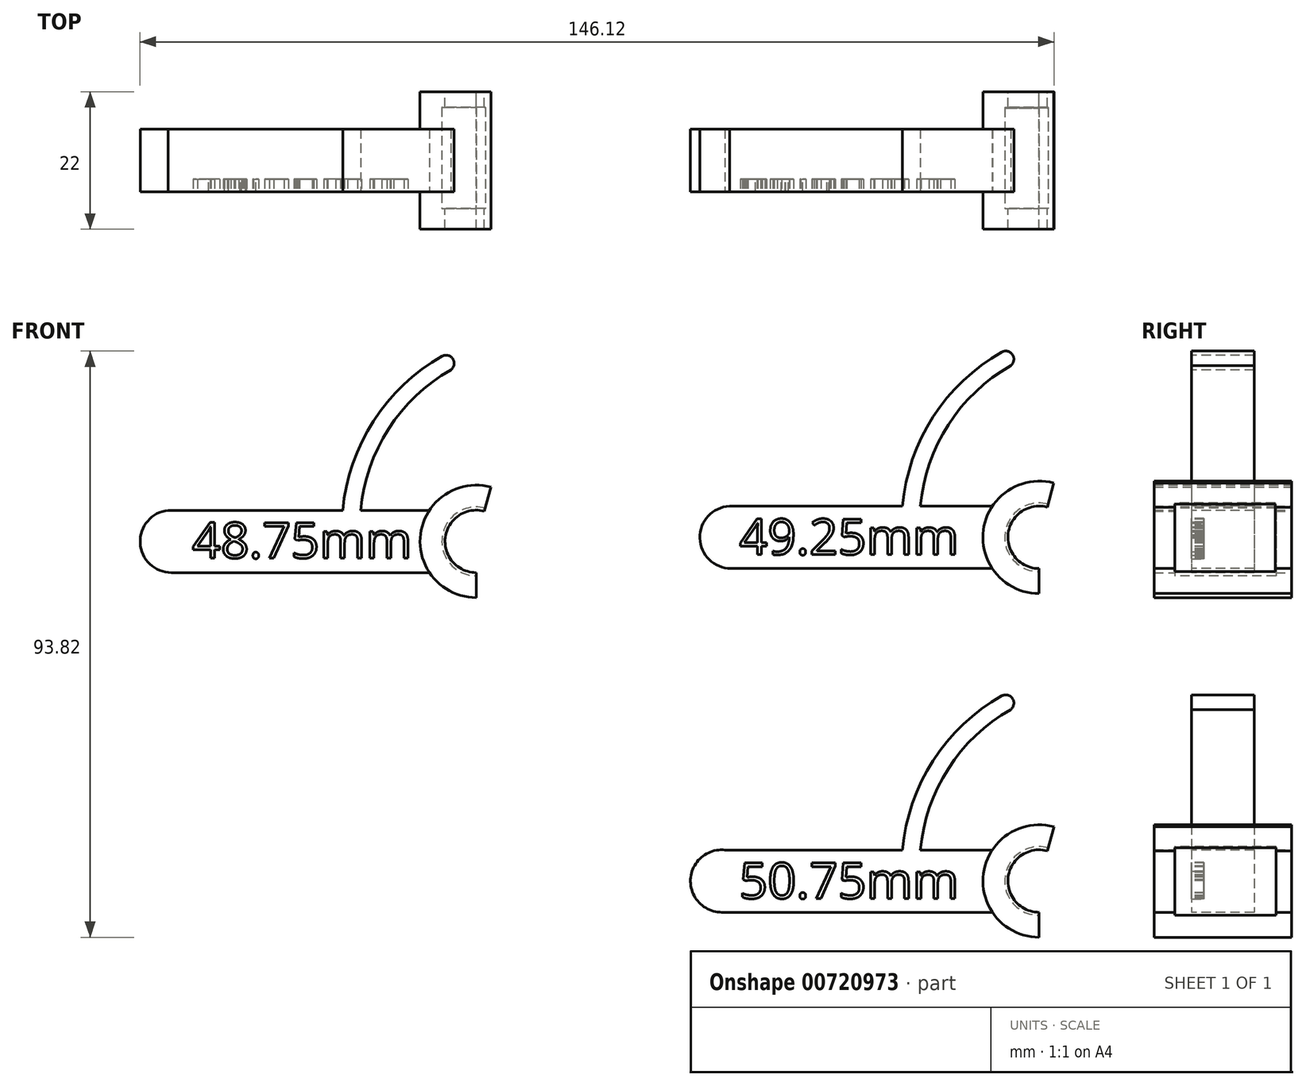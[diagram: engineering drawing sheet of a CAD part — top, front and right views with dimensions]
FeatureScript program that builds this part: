
annotation { "Feature Type Name" : "Feature", "Feature Type Description" : "" }
export const myFeature = defineFeature(function(context is Context, id is Id, definition is map)
    precondition{}
    {
        {
            var Q0;
            Q0=qCreatedBy(makeId("Front.planeOp"),FACE);
            var sketch = newSketch(context, id + "F0", { "sketchPlane" : qUnion([Q0])});
            skLineSegment(sketch, "E0.bottom", {"start": v(20.5, 25) * mm, "end": v(70.25, 25) * mm});
            skLineSegment(sketch, "E0.top", {"start": v(20.75, 15) * mm, "end": v(70, 15) * mm});
            skArc(sketch, "E1", {"start": v(20.5, 25) * mm, "mid": v(15.75, 19.88) * mm, "end": v(20.75, 15) * mm});
            skArc(sketch, "E2", {"start": v(71.29, 24.83) * mm, "mid": v(65.04, 20.65) * mm, "end": v(70, 15) * mm});
            skArc(sketch, "E3.0", {"start": v(72.32, 28.7) * mm, "mid": v(61.08, 21.17) * mm, "end": v(70, 11) * mm});
            skLineSegment(sketch, "E4", {"start": v(70.25, 29) * mm, "end": v(70.25, 25) * mm});
            skLineSegment(sketch, "E5", {"start": v(70, 15) * mm, "end": v(70, 11) * mm});
            skLineSegment(sketch, "E6.bottom", {"start": v(62.51, 25) * mm, "end": v(54.51, 25) * mm});
            skLineSegment(sketch, "E6.top", {"start": v(58.51, 37) * mm, "end": v(58.51, 37) * mm});
            skPoint(sketch, "E7.visualSharp", {"position": v(54.51, 37) * mm});
            skPoint(sketch, "E8.visualSharp", {"position": v(62.51, 37) * mm});
            skLineSegment(sketch, "E9", {"start": v(77.17, 20) * mm, "end": v(-0.92, 19.88) * mm, "construction": true});
            skPoint(sketch, "E9.endSnap0", {"position": v(15.75, 19.88) * mm});
            skLineSegment(sketch, "E10", {"start": v(70, 20) * mm, "end": v(72.32, 28.7) * mm});
            skArc(sketch, "E11", {"start": v(71.42, 25.31) * mm, "mid": v(64.55, 20.71) * mm, "end": v(70, 14.5) * mm});
            skArc(sketch, "E12", {"start": v(65.44, 47.47) * mm, "mid": v(55.47, 38) * mm, "end": v(51.02, 25) * mm});
            skArc(sketch, "E13", {"start": v(65.44, 47.47) * mm, "mid": v(65.74, 49.23) * mm, "end": v(64.01, 49.65) * mm});
            skArc(sketch, "E14", {"start": v(64.01, 49.65) * mm, "mid": v(53.04, 39.28) * mm, "end": v(48.15, 25) * mm});
            skLineSegment(sketch, "E15.bottom", {"start": v(19.75, -30.03) * mm, "end": v(69.5, -30.03) * mm});
            skLineSegment(sketch, "E15.top", {"start": v(19.24, -40) * mm, "end": v(70, -40) * mm});
            skArc(sketch, "E16", {"start": v(19.75, -30.03) * mm, "mid": v(14.25, -34.75) * mm, "end": v(19.24, -40) * mm});
            skArc(sketch, "E17", {"start": v(71.3, -30.17) * mm, "mid": v(65.04, -34.34) * mm, "end": v(70, -40) * mm});
            skArc(sketch, "E18.0", {"start": v(72.36, -26.31) * mm, "mid": v(61.08, -33.81) * mm, "end": v(70, -44) * mm});
            skLineSegment(sketch, "E19", {"start": v(70.25, -26) * mm, "end": v(69.5, -30.03) * mm});
            skLineSegment(sketch, "E20", {"start": v(70, -40) * mm, "end": v(70, -44) * mm});
            skLineSegment(sketch, "E21.bottom", {"start": v(62.5, -30.03) * mm, "end": v(54.5, -30.03) * mm});
            skLineSegment(sketch, "E21.top", {"start": v(17.58, -28.5) * mm, "end": v(17.58, -28.5) * mm});
            skPoint(sketch, "E22.visualSharp", {"position": v(54.5, -18.03) * mm});
            skPoint(sketch, "E23.visualSharp", {"position": v(62.5, -18.03) * mm});
            skLineSegment(sketch, "E24", {"start": v(77.17, -35) * mm, "end": v(-2.42, -34.75) * mm, "construction": true});
            skPoint(sketch, "E24.endSnap0", {"position": v(14.25, -34.75) * mm});
            skLineSegment(sketch, "E25", {"start": v(70, -35) * mm, "end": v(72.36, -26.31) * mm});
            skArc(sketch, "E26", {"start": v(71.44, -29.7) * mm, "mid": v(64.55, -34.27) * mm, "end": v(70, -40.5) * mm});
            skArc(sketch, "E27", {"start": v(65.44, -7.54) * mm, "mid": v(55.47, -17.01) * mm, "end": v(51.02, -30.03) * mm});
            skArc(sketch, "E28", {"start": v(65.44, -7.54) * mm, "mid": v(65.74, -5.79) * mm, "end": v(64.01, -5.37) * mm});
            skArc(sketch, "E29", {"start": v(64.01, -5.37) * mm, "mid": v(53.04, -15.74) * mm, "end": v(48.15, -30.03) * mm});
            skLineSegment(sketch, "E30.bottom", {"start": v(-69.25, 24.33) * mm, "end": v(-19.5, 24.33) * mm});
            skLineSegment(sketch, "E30.top", {"start": v(-68.76, 14.35) * mm, "end": v(-20, 14.35) * mm});
            skArc(sketch, "E31", {"start": v(-69.25, 24.33) * mm, "mid": v(-73.75, 19.1) * mm, "end": v(-68.76, 14.35) * mm});
            skArc(sketch, "E32", {"start": v(-18.7, 24.18) * mm, "mid": v(-24.96, 20) * mm, "end": v(-20, 14.35) * mm});
            skArc(sketch, "E33.0", {"start": v(-17.67, 28.04) * mm, "mid": v(-28.92, 20.53) * mm, "end": v(-20, 10.35) * mm});
            skLineSegment(sketch, "E34", {"start": v(-20, 14.35) * mm, "end": v(-20, 10.35) * mm});
            skLineSegment(sketch, "E35.bottom", {"start": v(-27.5, 24.33) * mm, "end": v(-35.5, 24.33) * mm});
            skLineSegment(sketch, "E35.top", {"start": v(-66.05, 60.12) * mm, "end": v(-66.05, 60.12) * mm});
            skPoint(sketch, "E36.visualSharp", {"position": v(-35.5, 36.33) * mm});
            skPoint(sketch, "E37.visualSharp", {"position": v(-27.5, 36.33) * mm});
            skPoint(sketch, "E38.endSnap0", {"position": v(-73.75, 19.1) * mm});
            skLineSegment(sketch, "E39", {"start": v(-20, 19.35) * mm, "end": v(-17.67, 28.04) * mm});
            skArc(sketch, "E40", {"start": v(-18.58, 24.66) * mm, "mid": v(-25.45, 20.07) * mm, "end": v(-20, 13.85) * mm});
            skArc(sketch, "E41", {"start": v(-24.06, 46.8) * mm, "mid": v(-34.04, 37.34) * mm, "end": v(-38.49, 24.33) * mm});
            skArc(sketch, "E42", {"start": v(-24.06, 46.8) * mm, "mid": v(-23.76, 48.56) * mm, "end": v(-25.5, 48.98) * mm});
            skArc(sketch, "E43", {"start": v(-25.5, 48.98) * mm, "mid": v(-36.46, 38.6) * mm, "end": v(-41.35, 24.33) * mm});
            skLineSegment(sketch, "E44", {"start": v(-15.27, 19.35) * mm, "end": v(-80.35, 19.35) * mm, "construction": true});
            skSolve(sketch);
        }
        {
            var Q0;
            {var subQ0=sQuery(id+"F0.wireOp",EDGE,"E5");Q0=makeQuery(id+"F0.imprint","IMPRINT",FACE,{"disambiguationData":[TD([[makeQuery(id+"F0.imprint","IMPRINT",EDGE,{"derivedFrom":subQ0}),-1.0]])]});}
            var Q1;
            {var subQ0=sQuery(id+"F0.wireOp",EDGE,"E2");Q1=makeQuery(id+"F0.imprint","IMPRINT",FACE,{"disambiguationData":[TD([[makeQuery(id+"F0.imprint","IMPRINT",EDGE,{"derivedFrom":subQ0}),-1.0]])]});}
            var Q2;
            {var subQ0=sQuery(id+"F0.wireOp",EDGE,"E4");Q2=makeQuery(id+"F0.imprint","IMPRINT",FACE,{"disambiguationData":[TD([[makeQuery(id+"F0.imprint","IMPRINT",EDGE,{"derivedFrom":subQ0}),-1.0]])]});}
            var Q3;
            {var subQ0=sQuery(id+"F0.wireOp",EDGE,"E10");var subQ1=sQuery(id+"F0.wireOp",EDGE,"E3.0");var subQ2=makeQuery(id+"F0.imprint","INTERSECT",VERTEX,{"derivedFrom":[subQ1,subQ0]});Q3=makeQuery(id+"F0.imprint","IMPRINT",FACE,{"disambiguationData":[TD([[makeQuery(id+"F0.imprint","IMPRINT",EDGE,{"disambiguationData":[TD([[subQ2,-1.0]])],"derivedFrom":subQ1}),1.0]])]});}
            var Q4;
            {var subQ0=sQuery(id+"F0.wireOp",EDGE,"E3.0");var subQ5=sQuery(id+"F0.wireOp",EDGE,"E0.top");var subQ6=makeQuery(id+"F0.imprint","INTERSECT",VERTEX,{"derivedFrom":[subQ5,subQ0]});Q4=makeQuery(id+"F0.imprint","IMPRINT",FACE,{"disambiguationData":[TD([[makeQuery(id+"F0.imprint","IMPRINT",EDGE,{"disambiguationData":[TD([[subQ6,-1.0]])],"derivedFrom":subQ5}),1.0]])]});}
            var Q5;
            {var subQ0=sQuery(id+"F0.wireOp",EDGE,"E3.0");var subQ1=sQuery(id+"F0.wireOp",EDGE,"E0.top");var subQ2=makeQuery(id+"F0.imprint","INTERSECT",VERTEX,{"derivedFrom":[subQ1,subQ0]});Q5=makeQuery(id+"F0.imprint","IMPRINT",FACE,{"disambiguationData":[TD([[makeQuery(id+"F0.imprint","IMPRINT",EDGE,{"disambiguationData":[TD([[subQ2,-1.0]])],"derivedFrom":subQ1}),-1.0]])]});}
            extrude(context, id + "F1", {"entities" : qUnion([Q0, Q1, Q2, Q3, Q4, Q5]), "depth" : 6 * mm, "offsetDistance" : 25 * mm, "hasSecondDirection" : true, "secondDirectionOppositeDirection" : true, "secondDirectionDepth" : 16 * mm});
        }
        {
            var Q0;
            {var subQ0=sQuery(id+"F0.wireOp",EDGE,"E1");Q0=makeQuery(id+"F0.imprint","IMPRINT",FACE,{"disambiguationData":[TD([[makeQuery(id+"F0.imprint","IMPRINT",EDGE,{"derivedFrom":subQ0}),1.0]])]});}
            var Q1;
            {var subQ0=sQuery(id+"F0.wireOp",EDGE,"E12");Q1=makeQuery(id+"F0.imprint","IMPRINT",FACE,{"disambiguationData":[TD([[makeQuery(id+"F0.imprint","IMPRINT",EDGE,{"derivedFrom":subQ0}),-1.0]])]});}
            extrude(context, id + "F2", {"entities" : qUnion([Q0, Q1]), "operationType" : NewBodyOperationType.ADD, "oppositeDirection" : true, "depth" : 10 * mm, "offsetDistance" : 25 * mm});
        }
        {
            var Q0;
            {var subQ0=sQuery(id+"F0.wireOp",EDGE,"E2");var subQ1=sQuery(id+"F0.wireOp",EDGE,"E0.bottom");var subQ2=makeQuery(id+"F0.imprint","INTERSECT",VERTEX,{"derivedFrom":[subQ1,subQ0]});Q0=makeQuery(id+"F0.imprint","IMPRINT",FACE,{"disambiguationData":[TD([[makeQuery(id+"F0.imprint","IMPRINT",EDGE,{"disambiguationData":[TD([[subQ2,1.0]])],"derivedFrom":subQ1}),-1.0]])]});}
            var Q1;
            {var subQ0=sQuery(id+"F0.wireOp",EDGE,"E5");var subQ3=sQuery(id+"F0.wireOp",EDGE,"E11");var subQ5=makeQuery(id+"F0.imprint","INTERSECT",VERTEX,{"derivedFrom":[subQ0,subQ3]});Q1=makeQuery(id+"F0.imprint","IMPRINT",FACE,{"disambiguationData":[TD([[makeQuery(id+"F0.imprint","IMPRINT",EDGE,{"disambiguationData":[TD([[subQ5,1.0]])],"derivedFrom":subQ3}),1.0]])]});}
            var Q2;
            {var subQ0=sQuery(id+"F0.wireOp",EDGE,"E2");var subQ1=sQuery(id+"F0.wireOp",EDGE,"E0.bottom");var subQ2=makeQuery(id+"F0.imprint","INTERSECT",VERTEX,{"derivedFrom":[subQ1,subQ0]});Q2=makeQuery(id+"F0.imprint","IMPRINT",FACE,{"disambiguationData":[TD([[makeQuery(id+"F0.imprint","IMPRINT",EDGE,{"disambiguationData":[TD([[subQ2,1.0]])],"derivedFrom":subQ1}),1.0]])]});}
            var Q3;
            {var subQ1=sQuery(id+"F0.wireOp",EDGE,"E2");var subQ3=sQuery(id+"F0.wireOp",EDGE,"E10");var subQ4=makeQuery(id+"F0.imprint","INTERSECT",VERTEX,{"derivedFrom":[subQ1,subQ3]});Q3=makeQuery(id+"F0.imprint","IMPRINT",FACE,{"disambiguationData":[TD([[makeQuery(id+"F0.imprint","IMPRINT",EDGE,{"disambiguationData":[TD([[subQ4,-1.0]])],"derivedFrom":subQ3}),1.0]])]});}
            extrude(context, id + "F3", {"entities" : qUnion([Q0, Q1, Q2, Q3]), "operationType" : NewBodyOperationType.REMOVE, "oppositeDirection" : true, "depth" : 13.4 * mm, "offsetDistance" : 25 * mm, "hasSecondDirection" : true, "secondDirectionOppositeDirection" : false, "secondDirectionDepth" : 2.7 * mm});
        }
        {
            var Q0;
            {var subQ3=sQuery(id+"F0.wireOp",EDGE,"E1");Q0=makeQuery(id+"F0.imprint","IMPRINT",FACE,{"disambiguationData":[TD([[makeQuery(id+"F0.imprint","IMPRINT",EDGE,{"derivedFrom":subQ3}),1.0]])]});}
            var sketch = newSketch(context, id + "F4", { "sketchPlane" : qUnion([Q0])});
            skText(sketch, "E45", { "text": "49.25mm", "fontName": "OpenSans-Regular.ttf"});
            const initialGuessF4  = {"E45": [0.02204, 0.01725, 1, 0, 0.00573]};
            skSetInitialGuess(sketch, initialGuessF4);
            skSolve(sketch);
        }
        {
            var Q0;
            Q0 = qSketchRegion(id + "F4", true);
            var Q1;
            Q1 = qConstructionFilter(qBodyType(qCreatedBy(id + "F4" ,EDGE), BodyType.WIRE), ConstructionObject.NO);
            extrude(context, id + "F5", {"entities" : qUnion([Q0]), "operationType" : NewBodyOperationType.REMOVE, "surfaceEntities" : qUnion([Q1]), "oppositeDirection" : true, "depth" : 2 * mm, "offsetDistance" : 25 * mm});
        }
        {
            var Q0;
            {var subQ0=sQuery(id+"F0.wireOp",EDGE,"E25");var subQ1=sQuery(id+"F0.wireOp",EDGE,"E18.0");var subQ2=makeQuery(id+"F0.imprint","INTERSECT",VERTEX,{"derivedFrom":[subQ1,subQ0]});Q0=makeQuery(id+"F0.imprint","IMPRINT",FACE,{"disambiguationData":[TD([[makeQuery(id+"F0.imprint","IMPRINT",EDGE,{"disambiguationData":[TD([[subQ2,-1.0]])],"derivedFrom":subQ1}),1.0]])]});}
            var Q1;
            {var subQ0=sQuery(id+"F0.wireOp",EDGE,"E18.0");var subQ5=sQuery(id+"F0.wireOp",EDGE,"E19");var subQ7=makeQuery(id+"F0.imprint","INTERSECT",VERTEX,{"derivedFrom":[subQ0,subQ5]});Q1=makeQuery(id+"F0.imprint","IMPRINT",FACE,{"disambiguationData":[TD([[makeQuery(id+"F0.imprint","IMPRINT",EDGE,{"disambiguationData":[TD([[subQ7,-1.0]])],"derivedFrom":subQ5}),-1.0]])]});}
            var Q2;
            {var subQ0=sQuery(id+"F0.wireOp",EDGE,"E18.0");var subQ5=sQuery(id+"F0.wireOp",EDGE,"E15.top");var subQ6=makeQuery(id+"F0.imprint","INTERSECT",VERTEX,{"derivedFrom":[subQ5,subQ0]});Q2=makeQuery(id+"F0.imprint","IMPRINT",FACE,{"disambiguationData":[TD([[makeQuery(id+"F0.imprint","IMPRINT",EDGE,{"disambiguationData":[TD([[subQ6,-1.0]])],"derivedFrom":subQ5}),1.0]])]});}
            var Q3;
            {var subQ0=sQuery(id+"F0.wireOp",EDGE,"E18.0");var subQ1=sQuery(id+"F0.wireOp",EDGE,"E15.top");var subQ2=makeQuery(id+"F0.imprint","INTERSECT",VERTEX,{"derivedFrom":[subQ1,subQ0]});Q3=makeQuery(id+"F0.imprint","IMPRINT",FACE,{"disambiguationData":[TD([[makeQuery(id+"F0.imprint","IMPRINT",EDGE,{"disambiguationData":[TD([[subQ2,-1.0]])],"derivedFrom":subQ1}),-1.0]])]});}
            var Q4;
            {var subQ0=sQuery(id+"F0.wireOp",EDGE,"E20");var subQ3=sQuery(id+"F0.wireOp",EDGE,"E26");var subQ5=makeQuery(id+"F0.imprint","INTERSECT",VERTEX,{"derivedFrom":[subQ0,subQ3]});Q4=makeQuery(id+"F0.imprint","IMPRINT",FACE,{"disambiguationData":[TD([[makeQuery(id+"F0.imprint","IMPRINT",EDGE,{"disambiguationData":[TD([[subQ5,1.0]])],"derivedFrom":subQ3}),1.0]])]});}
            var Q5;
            {var subQ1=sQuery(id+"F0.wireOp",EDGE,"E15.bottom");var subQ3=sQuery(id+"F0.wireOp",EDGE,"E26");var subQ4=makeQuery(id+"F0.imprint","INTERSECT",VERTEX,{"derivedFrom":[subQ1,subQ3]});Q5=makeQuery(id+"F0.imprint","IMPRINT",FACE,{"disambiguationData":[TD([[makeQuery(id+"F0.imprint","IMPRINT",EDGE,{"disambiguationData":[TD([[subQ4,-1.0]])],"derivedFrom":subQ3}),1.0]])]});}
            var Q6;
            {var subQ1=sQuery(id+"F0.wireOp",EDGE,"E15.bottom");var subQ3=sQuery(id+"F0.wireOp",EDGE,"E26");var subQ4=makeQuery(id+"F0.imprint","INTERSECT",VERTEX,{"derivedFrom":[subQ1,subQ3]});Q6=makeQuery(id+"F0.imprint","IMPRINT",FACE,{"disambiguationData":[TD([[makeQuery(id+"F0.imprint","IMPRINT",EDGE,{"disambiguationData":[TD([[subQ4,1.0]])],"derivedFrom":subQ3}),1.0]])]});}
            var Q7;
            {var subQ1=sQuery(id+"F0.wireOp",EDGE,"E17");var subQ3=sQuery(id+"F0.wireOp",EDGE,"E25");var subQ4=makeQuery(id+"F0.imprint","INTERSECT",VERTEX,{"derivedFrom":[subQ1,subQ3]});Q7=makeQuery(id+"F0.imprint","IMPRINT",FACE,{"disambiguationData":[TD([[makeQuery(id+"F0.imprint","IMPRINT",EDGE,{"disambiguationData":[TD([[subQ4,-1.0]])],"derivedFrom":subQ3}),1.0]])]});}
            extrude(context, id + "F6", {"entities" : qUnion([Q0, Q1, Q2, Q3, Q4, Q5, Q6, Q7]), "depth" : 6 * mm, "offsetDistance" : 25 * mm, "hasSecondDirection" : true, "secondDirectionOppositeDirection" : true, "secondDirectionDepth" : 16 * mm});
        }
        {
            var Q0;
            {var subQ7=sQuery(id+"F0.wireOp",EDGE,"E16");Q0=makeQuery(id+"F0.imprint","IMPRINT",FACE,{"disambiguationData":[TD([[makeQuery(id+"F0.imprint","IMPRINT",EDGE,{"derivedFrom":subQ7}),1.0]])]});}
            var Q1;
            {var subQ0=sQuery(id+"F0.wireOp",EDGE,"E27");Q1=makeQuery(id+"F0.imprint","IMPRINT",FACE,{"disambiguationData":[TD([[makeQuery(id+"F0.imprint","IMPRINT",EDGE,{"derivedFrom":subQ0}),-1.0]])]});}
            extrude(context, id + "F7", {"entities" : qUnion([Q0, Q1]), "operationType" : NewBodyOperationType.ADD, "oppositeDirection" : true, "depth" : 10 * mm, "offsetDistance" : 25 * mm});
        }
        {
            var Q0;
            {var subQ1=sQuery(id+"F0.wireOp",EDGE,"E17");var subQ3=sQuery(id+"F0.wireOp",EDGE,"E25");var subQ4=makeQuery(id+"F0.imprint","INTERSECT",VERTEX,{"derivedFrom":[subQ1,subQ3]});Q0=makeQuery(id+"F0.imprint","IMPRINT",FACE,{"disambiguationData":[TD([[makeQuery(id+"F0.imprint","IMPRINT",EDGE,{"disambiguationData":[TD([[subQ4,-1.0]])],"derivedFrom":subQ3}),1.0]])]});}
            var Q1;
            {var subQ1=sQuery(id+"F0.wireOp",EDGE,"E15.bottom");var subQ3=sQuery(id+"F0.wireOp",EDGE,"E26");var subQ4=makeQuery(id+"F0.imprint","INTERSECT",VERTEX,{"derivedFrom":[subQ1,subQ3]});Q1=makeQuery(id+"F0.imprint","IMPRINT",FACE,{"disambiguationData":[TD([[makeQuery(id+"F0.imprint","IMPRINT",EDGE,{"disambiguationData":[TD([[subQ4,1.0]])],"derivedFrom":subQ3}),1.0]])]});}
            var Q2;
            {var subQ1=sQuery(id+"F0.wireOp",EDGE,"E15.bottom");var subQ3=sQuery(id+"F0.wireOp",EDGE,"E26");var subQ4=makeQuery(id+"F0.imprint","INTERSECT",VERTEX,{"derivedFrom":[subQ1,subQ3]});Q2=makeQuery(id+"F0.imprint","IMPRINT",FACE,{"disambiguationData":[TD([[makeQuery(id+"F0.imprint","IMPRINT",EDGE,{"disambiguationData":[TD([[subQ4,-1.0]])],"derivedFrom":subQ3}),1.0]])]});}
            var Q3;
            {var subQ0=sQuery(id+"F0.wireOp",EDGE,"E20");var subQ3=sQuery(id+"F0.wireOp",EDGE,"E26");var subQ5=makeQuery(id+"F0.imprint","INTERSECT",VERTEX,{"derivedFrom":[subQ0,subQ3]});Q3=makeQuery(id+"F0.imprint","IMPRINT",FACE,{"disambiguationData":[TD([[makeQuery(id+"F0.imprint","IMPRINT",EDGE,{"disambiguationData":[TD([[subQ5,1.0]])],"derivedFrom":subQ3}),1.0]])]});}
            extrude(context, id + "F8", {"entities" : qUnion([Q0, Q1, Q2, Q3]), "operationType" : NewBodyOperationType.REMOVE, "oppositeDirection" : true, "depth" : 13.5 * mm, "offsetDistance" : 25 * mm, "hasSecondDirection" : true, "secondDirectionOppositeDirection" : false, "secondDirectionDepth" : 2.7 * mm});
        }
        {
            var Q0;
            {var subQ7=sQuery(id+"F0.wireOp",EDGE,"E16");Q0=makeQuery(id+"F0.imprint","IMPRINT",FACE,{"disambiguationData":[TD([[makeQuery(id+"F0.imprint","IMPRINT",EDGE,{"derivedFrom":subQ7}),1.0]])]});}
            var sketch = newSketch(context, id + "F9", { "sketchPlane" : qUnion([Q0])});
            skText(sketch, "E46", { "text": "50.75mm", "fontName": "OpenSans-Regular.ttf"});
            const initialGuessF9  = {"E46": [0.02204, -0.03778, 1, 0, 0.00573]};
            skSetInitialGuess(sketch, initialGuessF9);
            skSolve(sketch);
        }
        {
            var Q0;
            Q0 = qSketchRegion(id + "F9", true);
            extrude(context, id + "F10", {"entities" : qUnion([Q0]), "operationType" : NewBodyOperationType.REMOVE, "oppositeDirection" : true, "depth" : 2 * mm, "offsetDistance" : 25 * mm});
        }
        {
            var Q0;
            {var subQ0=sQuery(id+"F0.wireOp",EDGE,"E32");var subQ1=sQuery(id+"F0.wireOp",EDGE,"E30.bottom");var subQ3=makeQuery(id+"F0.imprint","INTERSECT",VERTEX,{"disambiguationData":[OD(1.0)],"derivedFrom":[subQ1,subQ0]});Q0=makeQuery(id+"F0.imprint","IMPRINT",FACE,{"disambiguationData":[TD([[makeQuery(id+"F0.imprint","IMPRINT",EDGE,{"disambiguationData":[TD([[subQ3,1.0]])],"derivedFrom":subQ1}),1.0]])]});}
            var Q1;
            {var subQ0=sQuery(id+"F0.wireOp",EDGE,"E32");var subQ1=sQuery(id+"F0.wireOp",EDGE,"E30.bottom");var subQ2=makeQuery(id+"F0.imprint","INTERSECT",VERTEX,{"disambiguationData":[OD(1.0)],"derivedFrom":[subQ1,subQ0]});Q1=makeQuery(id+"F0.imprint","IMPRINT",FACE,{"disambiguationData":[TD([[makeQuery(id+"F0.imprint","IMPRINT",EDGE,{"disambiguationData":[TD([[subQ2,1.0]])],"derivedFrom":subQ1}),-1.0]])]});}
            var Q2;
            {var subQ0=sQuery(id+"F0.wireOp",EDGE,"E34");var subQ3=sQuery(id+"F0.wireOp",EDGE,"E40");var subQ5=makeQuery(id+"F0.imprint","INTERSECT",VERTEX,{"derivedFrom":[subQ0,subQ3]});Q2=makeQuery(id+"F0.imprint","IMPRINT",FACE,{"disambiguationData":[TD([[makeQuery(id+"F0.imprint","IMPRINT",EDGE,{"disambiguationData":[TD([[subQ5,1.0]])],"derivedFrom":subQ3}),1.0]])]});}
            var Q3;
            {var subQ0=sQuery(id+"F0.wireOp",EDGE,"E33.0");var subQ1=sQuery(id+"F0.wireOp",EDGE,"E30.top");var subQ2=makeQuery(id+"F0.imprint","INTERSECT",VERTEX,{"derivedFrom":[subQ1,subQ0]});Q3=makeQuery(id+"F0.imprint","IMPRINT",FACE,{"disambiguationData":[TD([[makeQuery(id+"F0.imprint","IMPRINT",EDGE,{"disambiguationData":[TD([[subQ2,-1.0]])],"derivedFrom":subQ1}),-1.0]])]});}
            var Q4;
            {var subQ0=sQuery(id+"F0.wireOp",EDGE,"E33.0");var subQ5=sQuery(id+"F0.wireOp",EDGE,"E30.top");var subQ6=makeQuery(id+"F0.imprint","INTERSECT",VERTEX,{"derivedFrom":[subQ5,subQ0]});Q4=makeQuery(id+"F0.imprint","IMPRINT",FACE,{"disambiguationData":[TD([[makeQuery(id+"F0.imprint","IMPRINT",EDGE,{"disambiguationData":[TD([[subQ6,-1.0]])],"derivedFrom":subQ5}),1.0]])]});}
            var Q5;
            {var subQ0=sQuery(id+"F0.wireOp",EDGE,"E33.0");var subQ5=sQuery(id+"F0.wireOp",EDGE,"E39");var subQ6=makeQuery(id+"F0.imprint","INTERSECT",VERTEX,{"derivedFrom":[subQ0,subQ5]});Q5=makeQuery(id+"F0.imprint","IMPRINT",FACE,{"disambiguationData":[TD([[makeQuery(id+"F0.imprint","IMPRINT",EDGE,{"disambiguationData":[TD([[subQ6,1.0]])],"derivedFrom":subQ5}),1.0]])]});}
            extrude(context, id + "F11", {"entities" : qUnion([Q0, Q1, Q2, Q3, Q4, Q5]), "depth" : 6 * mm, "offsetDistance" : 25 * mm, "hasSecondDirection" : true, "secondDirectionOppositeDirection" : true, "secondDirectionDepth" : 16 * mm});
        }
        {
            var Q0;
            {var subQ3=sQuery(id+"F0.wireOp",EDGE,"E31");Q0=makeQuery(id+"F0.imprint","IMPRINT",FACE,{"disambiguationData":[TD([[makeQuery(id+"F0.imprint","IMPRINT",EDGE,{"derivedFrom":subQ3}),1.0]])]});}
            var Q1;
            {var subQ0=sQuery(id+"F0.wireOp",EDGE,"E41");Q1=makeQuery(id+"F0.imprint","IMPRINT",FACE,{"disambiguationData":[TD([[makeQuery(id+"F0.imprint","IMPRINT",EDGE,{"derivedFrom":subQ0}),-1.0]])]});}
            extrude(context, id + "F12", {"entities" : qUnion([Q0, Q1]), "operationType" : NewBodyOperationType.ADD, "oppositeDirection" : true, "depth" : 10 * mm, "offsetDistance" : 25 * mm});
        }
        {
            var Q0;
            {var subQ0=sQuery(id+"F0.wireOp",EDGE,"E34");var subQ3=sQuery(id+"F0.wireOp",EDGE,"E40");var subQ5=makeQuery(id+"F0.imprint","INTERSECT",VERTEX,{"derivedFrom":[subQ0,subQ3]});Q0=makeQuery(id+"F0.imprint","IMPRINT",FACE,{"disambiguationData":[TD([[makeQuery(id+"F0.imprint","IMPRINT",EDGE,{"disambiguationData":[TD([[subQ5,1.0]])],"derivedFrom":subQ3}),1.0]])]});}
            var Q1;
            {var subQ0=sQuery(id+"F0.wireOp",EDGE,"E32");var subQ1=sQuery(id+"F0.wireOp",EDGE,"E30.bottom");var subQ2=makeQuery(id+"F0.imprint","INTERSECT",VERTEX,{"disambiguationData":[OD(1.0)],"derivedFrom":[subQ1,subQ0]});Q1=makeQuery(id+"F0.imprint","IMPRINT",FACE,{"disambiguationData":[TD([[makeQuery(id+"F0.imprint","IMPRINT",EDGE,{"disambiguationData":[TD([[subQ2,1.0]])],"derivedFrom":subQ1}),-1.0]])]});}
            var Q2;
            {var subQ0=sQuery(id+"F0.wireOp",EDGE,"E32");var subQ1=sQuery(id+"F0.wireOp",EDGE,"E30.bottom");var subQ3=makeQuery(id+"F0.imprint","INTERSECT",VERTEX,{"disambiguationData":[OD(1.0)],"derivedFrom":[subQ1,subQ0]});Q2=makeQuery(id+"F0.imprint","IMPRINT",FACE,{"disambiguationData":[TD([[makeQuery(id+"F0.imprint","IMPRINT",EDGE,{"disambiguationData":[TD([[subQ3,1.0]])],"derivedFrom":subQ1}),1.0]])]});}
            extrude(context, id + "F13", {"entities" : qUnion([Q0, Q1, Q2]), "operationType" : NewBodyOperationType.REMOVE, "oppositeDirection" : true, "depth" : 13.5 * mm, "offsetDistance" : 25 * mm, "hasSecondDirection" : true, "secondDirectionOppositeDirection" : false, "secondDirectionDepth" : 2.7 * mm});
        }
        {
            var Q0;
            {var subQ3=sQuery(id+"F0.wireOp",EDGE,"E31");Q0=makeQuery(id+"F0.imprint","IMPRINT",FACE,{"disambiguationData":[TD([[makeQuery(id+"F0.imprint","IMPRINT",EDGE,{"derivedFrom":subQ3}),1.0]])]});}
            var sketch = newSketch(context, id + "F14", { "sketchPlane" : qUnion([Q0])});
            skText(sketch, "E47", { "text": "48.75mm", "fontName": "OpenSans-Regular.ttf"});
            const initialGuessF14  = {"E47": [-0.06542, 0.01668, 1, 0, 0.00573]};
            skSetInitialGuess(sketch, initialGuessF14);
            skSolve(sketch);
        }
        {
            var Q0;
            Q0 = qSketchRegion(id + "F14", true);
            extrude(context, id + "F15", {"entities" : qUnion([Q0]), "operationType" : NewBodyOperationType.REMOVE, "oppositeDirection" : true, "depth" : 2 * mm, "offsetDistance" : 25 * mm});
        }
    });
